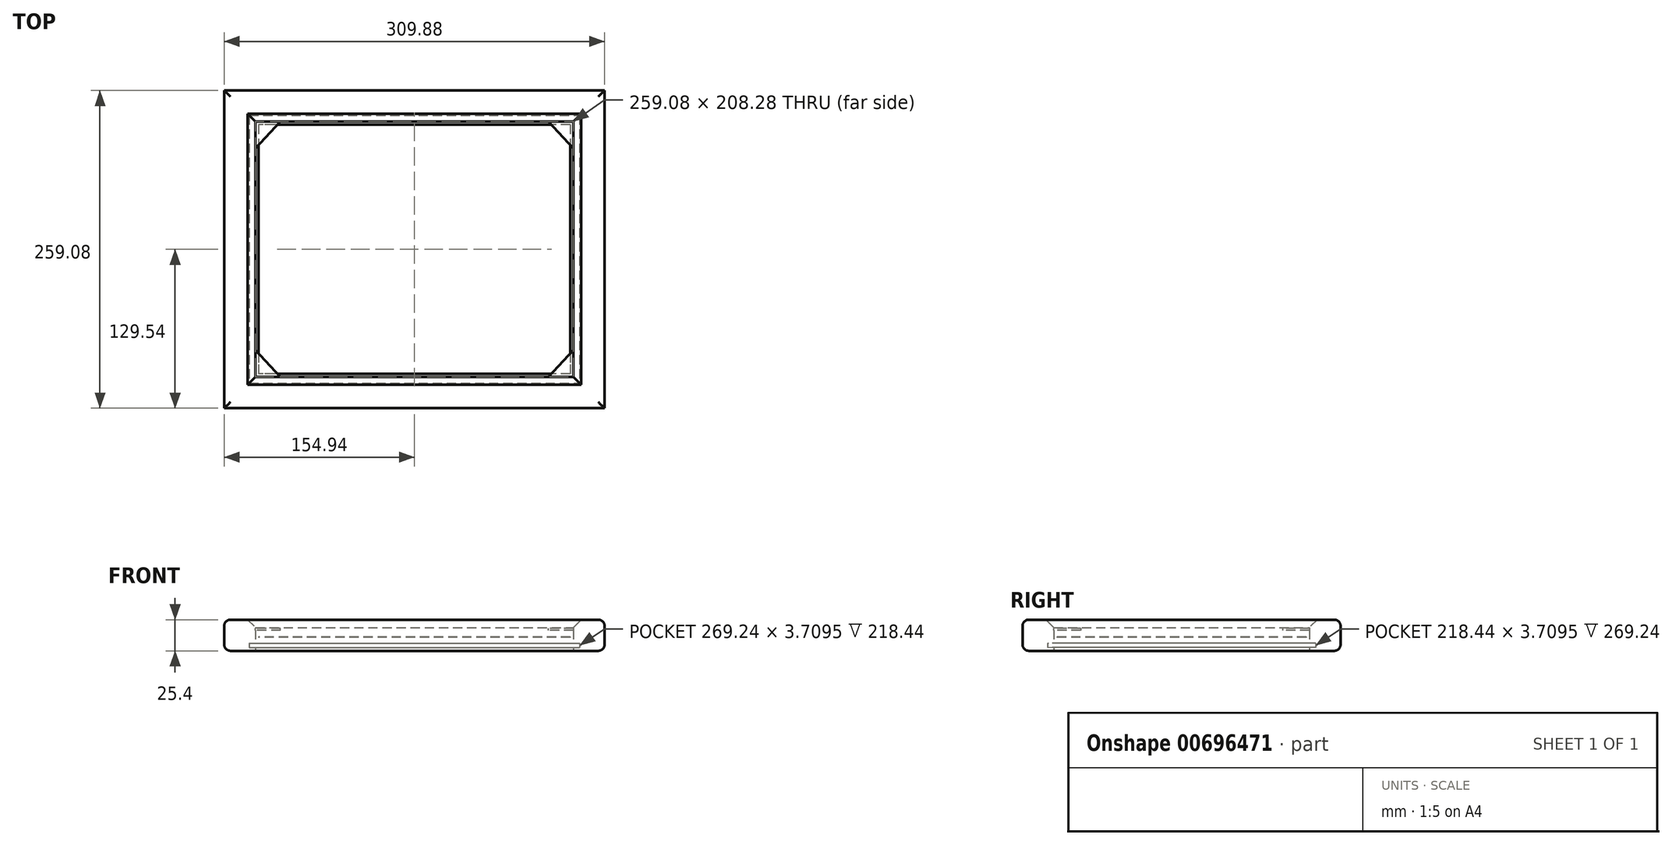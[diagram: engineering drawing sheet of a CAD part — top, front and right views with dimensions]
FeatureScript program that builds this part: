
annotation { "Feature Type Name" : "Feature", "Feature Type Description" : "" }
export const myFeature = defineFeature(function(context is Context, id is Id, definition is map)
    precondition{}
    {
        {
            var Q0;
            Q0=qCreatedBy(makeId("Top.planeOp"),FACE);
            var sketch = newSketch(context, id + "F0", { "sketchPlane" : qUnion([Q0])});
            skLineSegment(sketch, "E0.bottom", {"start": v(127, 101.6) * mm, "end": v(-127, 101.6) * mm});
            skLineSegment(sketch, "E0.top", {"start": v(127, -101.6) * mm, "end": v(-127, -101.6) * mm});
            skLineSegment(sketch, "E0.left", {"start": v(127, 101.6) * mm, "end": v(127, -101.6) * mm});
            skLineSegment(sketch, "E0.right", {"start": v(-127, 101.6) * mm, "end": v(-127, -101.6) * mm});
            skPoint(sketch, "E0.middle", {"position": v(0, 0) * mm});
            skLineSegment(sketch, "E1.0", {"start": v(129.54, 104.14) * mm, "end": v(-129.54, 104.14) * mm});
            skLineSegment(sketch, "E1.1", {"start": v(129.54, 104.14) * mm, "end": v(129.54, -104.14) * mm});
            skLineSegment(sketch, "E1.2", {"start": v(129.54, -104.14) * mm, "end": v(-129.54, -104.14) * mm});
            skLineSegment(sketch, "E1.3", {"start": v(-129.54, 104.14) * mm, "end": v(-129.54, -104.14) * mm});
            skLineSegment(sketch, "E2.0", {"start": v(154.94, 129.54) * mm, "end": v(-154.94, 129.54) * mm});
            skLineSegment(sketch, "E2.1", {"start": v(154.94, 129.54) * mm, "end": v(154.94, -129.54) * mm});
            skLineSegment(sketch, "E2.2", {"start": v(154.94, -129.54) * mm, "end": v(-154.94, -129.54) * mm});
            skLineSegment(sketch, "E2.3", {"start": v(-154.94, 129.54) * mm, "end": v(-154.94, -129.54) * mm});
            skSolve(sketch);
        }
        {
            var Q0;
            Q0=makeQuery(id+"F0.imprint","IMPRINT",FACE,{"disambiguationData":[TD([[makeQuery(id+"F0.imprint","IMPRINT",EDGE,{"derivedFrom":sQuery(id+"F0.wireOp",EDGE,"E0.bottom")}),1.0]])]});
            extrude(context, id + "F1", {"entities" : qUnion([Q0]), "depth" : 0.25 * mm, "offsetDistance" : 25.4 * mm});
        }
        {
            var Q0;
            Q0=makeQuery(id+"F0.imprint","IMPRINT",FACE,{"disambiguationData":[TD([[makeQuery(id+"F0.imprint","IMPRINT",EDGE,{"derivedFrom":sQuery(id+"F0.wireOp",EDGE,"E1.0")}),-1.0]])]});
            extrude(context, id + "F2", {"entities" : qUnion([Q0]), "depth" : 25.4 * mm, "offsetDistance" : 25.4 * mm});
        }
        {
            var Q0;
            Q0=makeQuery(id+"F2.opExtrude","CAP_EDGE",EDGE,{"disambiguationData":[OSD([sQuery(id+"F0.wireOp",EDGE,"E1.0")])],"isStart":false});
            var Q1;
            Q1=makeQuery(id+"F2.opExtrude","CAP_EDGE",EDGE,{"disambiguationData":[OSD([sQuery(id+"F0.wireOp",EDGE,"E1.3")])],"isStart":false});
            var Q2;
            Q2=makeQuery(id+"F2.opExtrude","CAP_EDGE",EDGE,{"disambiguationData":[OSD([sQuery(id+"F0.wireOp",EDGE,"E1.1")])],"isStart":false});
            var Q3;
            Q3=makeQuery(id+"F2.opExtrude","CAP_EDGE",EDGE,{"disambiguationData":[OSD([sQuery(id+"F0.wireOp",EDGE,"E1.2")])],"isStart":false});
            chamfer(context, id + "F3", {"entities" : qUnion([Q0, Q1, Q2, Q3]), "width" : 6.35 * mm, "tangentPropagation" : true});
        }
        {
            var Q0;
            Q0=makeQuery(id+"F1.opExtrude","SWEPT_BODY",BODY,{"disambiguationData":[OSD([sQuery(id+"F0.wireOp",EDGE,"E0.bottom"),sQuery(id+"F0.wireOp",EDGE,"E0.top"),sQuery(id+"F0.wireOp",EDGE,"E0.left"),sQuery(id+"F0.wireOp",EDGE,"E0.right")])]});
            transform(context, id + "F4", {"entities" : qUnion([Q0]), "transformType" : TransformType.TRANSLATION_3D, "dx" : 0 * mm, "dy" : 0 * mm, "dz" : 10.92 * mm, "makeCopy" : false});
        }
        {
            var Q0;
            Q0=makeQuery(id+"F2.opExtrude","CAP_EDGE",EDGE,{"disambiguationData":[OSD([sQuery(id+"F0.wireOp",EDGE,"E2.3")])],"isStart":false});
            var Q1;
            Q1=makeQuery(id+"F2.opExtrude","CAP_EDGE",EDGE,{"disambiguationData":[OSD([sQuery(id+"F0.wireOp",EDGE,"E2.2")])],"isStart":false});
            var Q2;
            Q2=makeQuery(id+"F2.opExtrude","CAP_EDGE",EDGE,{"disambiguationData":[OSD([sQuery(id+"F0.wireOp",EDGE,"E2.1")])],"isStart":false});
            var Q3;
            Q3=makeQuery(id+"F2.opExtrude","CAP_EDGE",EDGE,{"disambiguationData":[OSD([sQuery(id+"F0.wireOp",EDGE,"E2.0")])],"isStart":false});
            var Q4;
            Q4=makeQuery(id+"F2.opExtrude","CAP_EDGE",EDGE,{"disambiguationData":[OSD([sQuery(id+"F0.wireOp",EDGE,"E2.1")])],"isStart":true});
            var Q5;
            Q5=makeQuery(id+"F2.opExtrude","CAP_EDGE",EDGE,{"disambiguationData":[OSD([sQuery(id+"F0.wireOp",EDGE,"E2.2")])],"isStart":true});
            var Q6;
            Q6=makeQuery(id+"F2.opExtrude","CAP_EDGE",EDGE,{"disambiguationData":[OSD([sQuery(id+"F0.wireOp",EDGE,"E2.3")])],"isStart":true});
            var Q7;
            Q7=makeQuery(id+"F2.opExtrude","CAP_EDGE",EDGE,{"disambiguationData":[OSD([sQuery(id+"F0.wireOp",EDGE,"E2.0")])],"isStart":true});
            fillet(context, id + "F5", {"entities" : qUnion([Q0, Q1, Q2, Q3, Q4, Q5, Q6, Q7]), "radius" : 5.08 * mm, "tangentPropagation" : true, "allowEdgeOverflow" : false});
        }
        {
            var Q0;
            Q0=makeQuery(id+"F2.opExtrude","SWEPT_FACE",FACE,{"disambiguationData":[OSD([sQuery(id+"F0.wireOp",EDGE,"E1.0")])]});
            var sketch = newSketch(context, id + "F6", { "sketchPlane" : qUnion([Q0])});
            skLineSegment(sketch, "E3.bottom", {"start": v(-129.54, 2.59) * mm, "end": v(129.54, 2.59) * mm});
            skLineSegment(sketch, "E3.top", {"start": v(-129.54, 6.3) * mm, "end": v(129.54, 6.3) * mm});
            skLineSegment(sketch, "E3.left", {"start": v(-129.54, 2.59) * mm, "end": v(-129.54, 6.3) * mm});
            skLineSegment(sketch, "E3.right", {"start": v(129.54, 2.59) * mm, "end": v(129.54, 6.3) * mm});
            skSolve(sketch);
        }
        {
            var Q0;
            Q0 = qSketchRegion(id + "F6", true);
            extrude(context, id + "F7", {"entities" : qUnion([Q0]), "operationType" : NewBodyOperationType.REMOVE, "oppositeDirection" : true, "depth" : 5.08 * mm, "offsetDistance" : 25.4 * mm});
        }
        {
            var Q0;
            Q0=makeQuery(id+"F7.boolean.opBoolean","MERGE",FACE,{"derivedFrom":[makeQuery(id+"F2.opExtrude","SWEPT_FACE",FACE,{"disambiguationData":[OSD([sQuery(id+"F0.wireOp",EDGE,"E1.3")])]}),makeQuery(id+"F7.opExtrude","SWEPT_FACE",FACE,{"disambiguationData":[OSD([sQuery(id+"F6.wireOp",EDGE,"E3.left")])]})]});
            var sketch = newSketch(context, id + "F8", { "sketchPlane" : qUnion([Q0])});
            skLineSegment(sketch, "E4", {"start": v(109.22, 6.3) * mm, "end": v(109.22, 2.59) * mm});
            skLineSegment(sketch, "E5", {"start": v(109.22, 2.59) * mm, "end": v(-104.14, 2.59) * mm});
            skLineSegment(sketch, "E6", {"start": v(-104.14, 2.59) * mm, "end": v(-104.14, 6.3) * mm});
            skLineSegment(sketch, "E7", {"start": v(-104.14, 6.3) * mm, "end": v(109.22, 6.3) * mm});
            skSolve(sketch);
        }
        {
            var Q0;
            Q0 = qSketchRegion(id + "F8", true);
            extrude(context, id + "F9", {"entities" : qUnion([Q0]), "operationType" : NewBodyOperationType.REMOVE, "oppositeDirection" : true, "depth" : 5.08 * mm, "offsetDistance" : 25.4 * mm});
        }
        {
            var Q0;
            Q0=makeQuery(id+"F9.boolean.opBoolean","MERGE",FACE,{"derivedFrom":[makeQuery(id+"F2.opExtrude","SWEPT_FACE",FACE,{"disambiguationData":[OSD([sQuery(id+"F0.wireOp",EDGE,"E1.2")])]}),makeQuery(id+"F9.opExtrude","SWEPT_FACE",FACE,{"disambiguationData":[OSD([sQuery(id+"F8.wireOp",EDGE,"E6")])]})]});
            var sketch = newSketch(context, id + "F10", { "sketchPlane" : qUnion([Q0])});
            skLineSegment(sketch, "E8", {"start": v(134.62, 6.3) * mm, "end": v(134.62, 2.59) * mm});
            skLineSegment(sketch, "E9", {"start": v(134.62, 2.59) * mm, "end": v(-129.54, 2.59) * mm});
            skLineSegment(sketch, "E10", {"start": v(-129.54, 2.59) * mm, "end": v(-129.54, 6.3) * mm});
            skLineSegment(sketch, "E11", {"start": v(-129.54, 6.3) * mm, "end": v(134.62, 6.3) * mm});
            skSolve(sketch);
        }
        {
            var Q0;
            Q0 = qSketchRegion(id + "F10", true);
            extrude(context, id + "F11", {"entities" : qUnion([Q0]), "operationType" : NewBodyOperationType.REMOVE, "oppositeDirection" : true, "depth" : 5.08 * mm, "offsetDistance" : 25.4 * mm});
        }
        {
            var Q0;
            Q0=makeQuery(id+"F11.boolean.opBoolean","MERGE",FACE,{"derivedFrom":[makeQuery(id+"F7.boolean.opBoolean","MERGE",FACE,{"derivedFrom":[makeQuery(id+"F2.opExtrude","SWEPT_FACE",FACE,{"disambiguationData":[OSD([sQuery(id+"F0.wireOp",EDGE,"E1.1")])]}),makeQuery(id+"F7.opExtrude","SWEPT_FACE",FACE,{"disambiguationData":[OSD([sQuery(id+"F6.wireOp",EDGE,"E3.right")])]})]}),makeQuery(id+"F11.opExtrude","SWEPT_FACE",FACE,{"disambiguationData":[OSD([sQuery(id+"F10.wireOp",EDGE,"E10")])]})]});
            var sketch = newSketch(context, id + "F12", { "sketchPlane" : qUnion([Q0])});
            skLineSegment(sketch, "E12", {"start": v(-109.22, 6.3) * mm, "end": v(109.22, 6.3) * mm});
            skLineSegment(sketch, "E13", {"start": v(109.22, 6.3) * mm, "end": v(109.22, 2.59) * mm});
            skLineSegment(sketch, "E14", {"start": v(109.22, 2.59) * mm, "end": v(-109.22, 2.59) * mm});
            skLineSegment(sketch, "E15", {"start": v(-109.22, 2.59) * mm, "end": v(-109.22, 6.3) * mm});
            skSolve(sketch);
        }
        {
            var Q0;
            Q0 = qSketchRegion(id + "F12", true);
            extrude(context, id + "F13", {"entities" : qUnion([Q0]), "operationType" : NewBodyOperationType.REMOVE, "oppositeDirection" : true, "depth" : 5.08 * mm, "offsetDistance" : 25.4 * mm});
        }
        {
            var Q0;
            Q0=makeQuery(id+"F1.opExtrude","CAP_FACE",FACE,{"disambiguationData":[OSD([sQuery(id+"F0.wireOp",EDGE,"E0.bottom"),sQuery(id+"F0.wireOp",EDGE,"E0.top"),sQuery(id+"F0.wireOp",EDGE,"E0.left"),sQuery(id+"F0.wireOp",EDGE,"E0.right")])],"isStart":false});
            cPlane(context, id + "F14", {"entities" : qUnion([Q0]), "cplaneType" : CPlaneType.OFFSET, "offset" : 7.11 * mm, "width" : 152.4 * mm, "height" : 152.4 * mm});
        }
        {
            var Q0;
            Q0=qCreatedBy(id+"F14.planeOp",FACE);
            var sketch = newSketch(context, id + "F15", { "sketchPlane" : qUnion([Q0])});
            skLineSegment(sketch, "E16", {"start": v(-107.9, 105.56) * mm, "end": v(-131.1, 80.52) * mm});
            skLineSegment(sketch, "E17", {"start": v(-131.1, 80.52) * mm, "end": v(-132.73, 109.34) * mm});
            skLineSegment(sketch, "E18", {"start": v(-132.73, 109.34) * mm, "end": v(-107.9, 105.56) * mm});
            skLineSegment(sketch, "E19", {"start": v(0, 0) * mm, "end": v(-147.68, 0) * mm});
            skLineSegment(sketch, "E20", {"start": v(0, 0) * mm, "end": v(0, 93.61) * mm});
            skLineSegment(sketch, "E21.MirrorCS", {"start": v(-107.9, -105.56) * mm, "end": v(-131.1, -80.52) * mm});
            skLineSegment(sketch, "E22.MirrorCS", {"start": v(-132.73, -109.34) * mm, "end": v(-107.9, -105.56) * mm});
            skLineSegment(sketch, "E23.MirrorCS", {"start": v(-131.1, -80.52) * mm, "end": v(-132.73, -109.34) * mm});
            skLineSegment(sketch, "E24.MirrorCS", {"start": v(107.9, 105.56) * mm, "end": v(131.1, 80.52) * mm});
            skLineSegment(sketch, "E25.MirrorCS", {"start": v(132.73, 109.34) * mm, "end": v(107.9, 105.56) * mm});
            skLineSegment(sketch, "E26.MirrorCS", {"start": v(131.1, 80.52) * mm, "end": v(132.73, 109.34) * mm});
            skLineSegment(sketch, "E27.MirrorCS", {"start": v(107.9, -105.56) * mm, "end": v(131.1, -80.52) * mm});
            skLineSegment(sketch, "E28.MirrorCS", {"start": v(131.1, -80.52) * mm, "end": v(132.73, -109.34) * mm});
            skLineSegment(sketch, "E29.MirrorCS", {"start": v(132.73, -109.34) * mm, "end": v(107.9, -105.56) * mm});
            skSolve(sketch);
        }
        {
            var Q0;
            Q0 = qSketchRegion(id + "F15", true);
            extrude(context, id + "F16", {"entities" : qUnion([Q0]), "operationType" : NewBodyOperationType.ADD, "oppositeDirection" : true, "depth" : 1.52 * mm, "offsetDistance" : 25.4 * mm});
        }
    });
